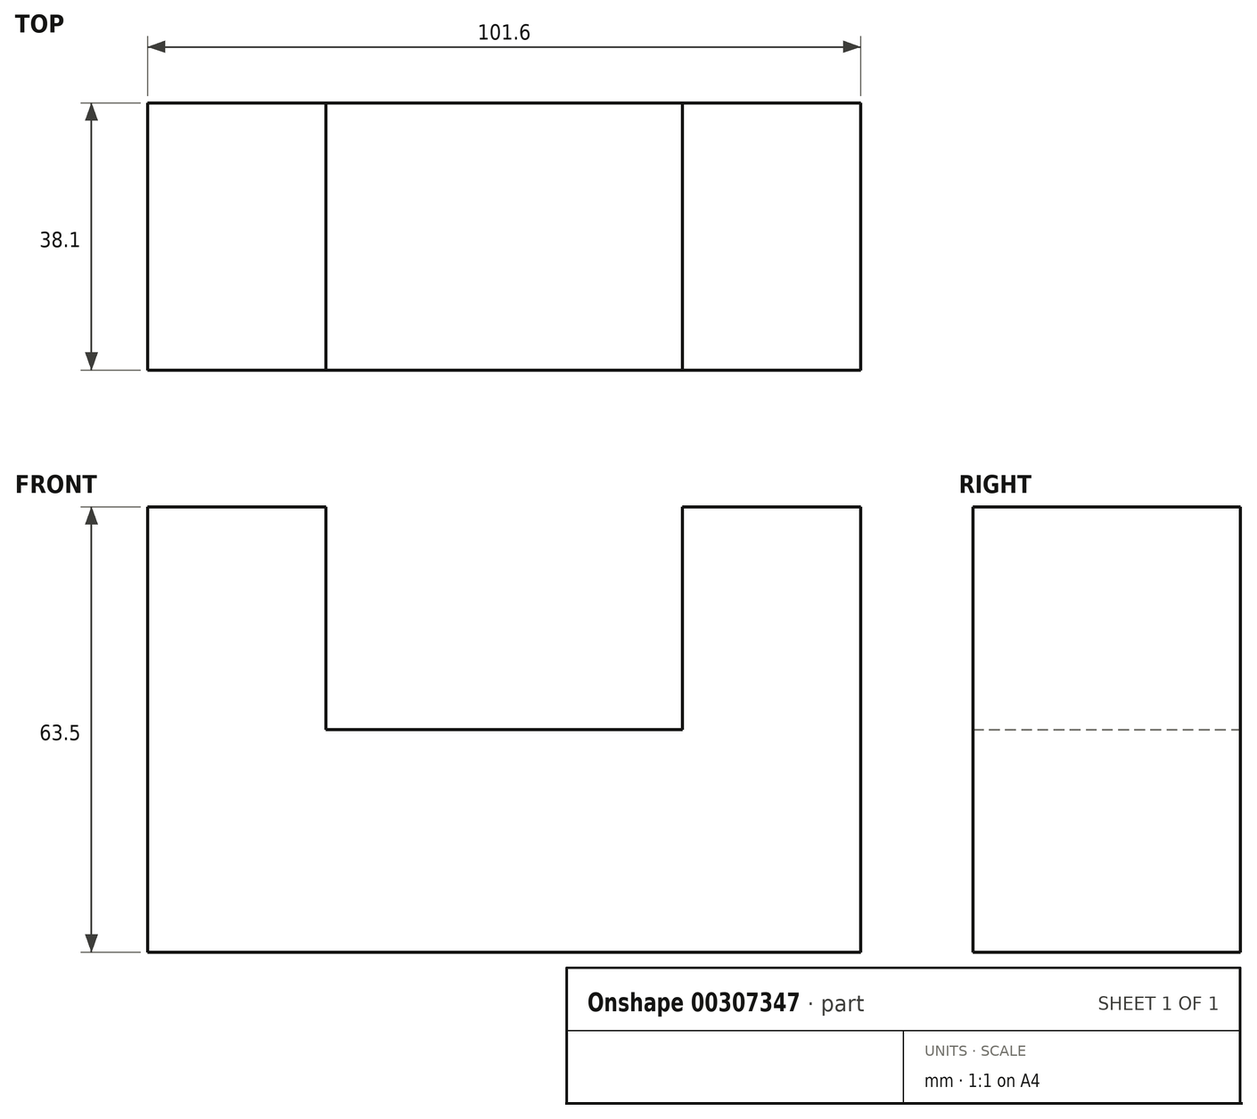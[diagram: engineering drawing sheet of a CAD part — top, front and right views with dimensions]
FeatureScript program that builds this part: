
annotation { "Feature Type Name" : "Feature", "Feature Type Description" : "" }
export const myFeature = defineFeature(function(context is Context, id is Id, definition is map)
    precondition{}
    {
        {
            var Q0;
            Q0=qCreatedBy(makeId("Front.planeOp"),FACE);
            var sketch = newSketch(context, id + "F0", { "sketchPlane" : qUnion([Q0])});
            skLineSegment(sketch, "E0", {"start": v(-45.34, -9.23) * mm, "end": v(56.26, -9.23) * mm});
            skLineSegment(sketch, "E1", {"start": v(56.26, -9.23) * mm, "end": v(56.26, 54.27) * mm});
            skLineSegment(sketch, "E2", {"start": v(56.26, 54.27) * mm, "end": v(30.86, 54.27) * mm});
            skLineSegment(sketch, "E3", {"start": v(30.86, 54.27) * mm, "end": v(30.86, 22.52) * mm});
            skLineSegment(sketch, "E4", {"start": v(30.86, 22.52) * mm, "end": v(-19.94, 22.52) * mm});
            skLineSegment(sketch, "E5", {"start": v(-19.94, 22.52) * mm, "end": v(-19.94, 54.27) * mm});
            skLineSegment(sketch, "E6", {"start": v(-19.94, 54.27) * mm, "end": v(-45.34, 54.27) * mm});
            skLineSegment(sketch, "E7", {"start": v(-45.34, 54.27) * mm, "end": v(-45.34, -9.23) * mm});
            skSolve(sketch);
        }
        {
            var Q0;
            Q0 = qSketchRegion(id + "F0", true);
            extrude(context, id + "F1", {"entities" : qUnion([Q0]), "depth" : 38.1 * mm});
        }
    });
